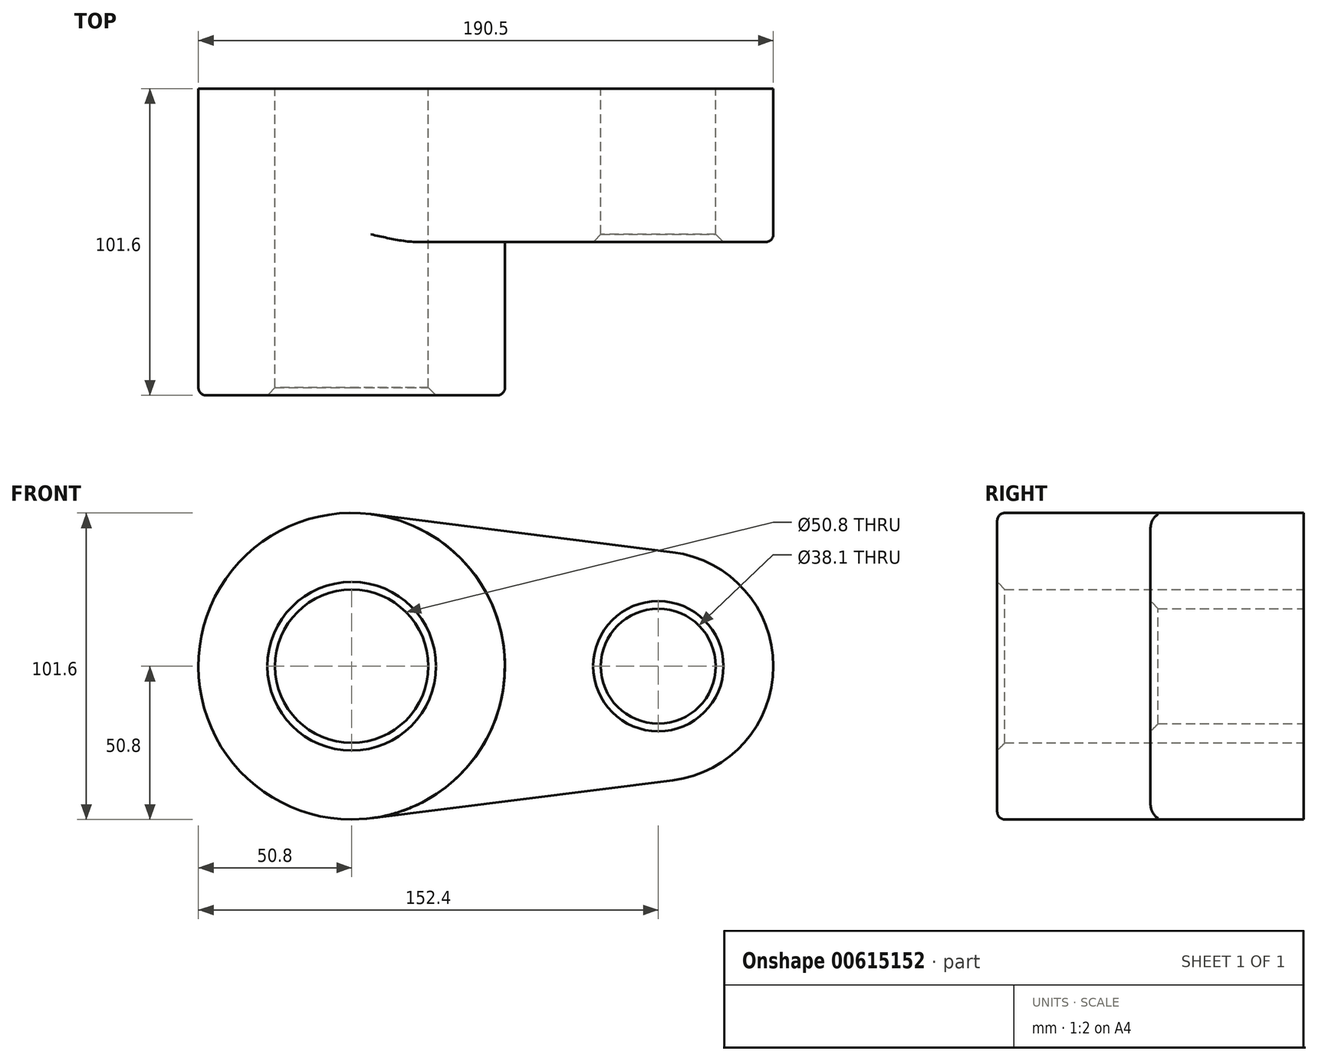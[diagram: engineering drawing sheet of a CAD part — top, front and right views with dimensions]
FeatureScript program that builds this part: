
annotation { "Feature Type Name" : "Feature", "Feature Type Description" : "" }
export const myFeature = defineFeature(function(context is Context, id is Id, definition is map)
    precondition{}
    {
        {
            var Q0;
            Q0=qCreatedBy(makeId("Front.planeOp"),FACE);
            var sketch = newSketch(context, id + "F0", { "sketchPlane" : qUnion([Q0])});
            skCircle(sketch, "E0", {"center": v(0, 0) * mm, "radius": 50.8 * mm});
            skCircle(sketch, "E1", {"center": v(101.6, 0) * mm, "radius": 38.1 * mm});
            skLineSegment(sketch, "E2", {"start": v(6.35, 50.4) * mm, "end": v(106.36, 37.8) * mm});
            skLineSegment(sketch, "E3", {"start": v(6.35, -50.4) * mm, "end": v(106.36, -37.8) * mm});
            skCircle(sketch, "E4", {"center": v(0, 0) * mm, "radius": 25.4 * mm});
            skCircle(sketch, "E5", {"center": v(101.6, 0) * mm, "radius": 19.05 * mm});
            skSolve(sketch);
        }
        {
            var Q0;
            Q0 = qSketchRegion(id + "F0", true);
            extrude(context, id + "F1", {"entities" : qUnion([Q0]), "depth" : 50.8 * mm, "offsetDistance" : 25.4 * mm});
        }
        {
            var Q0;
            Q0=makeQuery(id+"F0.imprint","IMPRINT",FACE,{"disambiguationData":[TD([[makeQuery(id+"F0.imprint","IMPRINT",EDGE,{"derivedFrom":sQuery(id+"F0.wireOp",EDGE,"E4")}),-1.0]])]});
            extrude(context, id + "F2", {"entities" : qUnion([Q0]), "operationType" : NewBodyOperationType.ADD, "depth" : 101.6 * mm, "offsetDistance" : 25.4 * mm});
        }
        {
            var Q0;
            Q0=makeQuery(id+"F1.opExtrude","CAP_EDGE",EDGE,{"disambiguationData":[OSD([sQuery(id+"F0.wireOp",EDGE,"E3")])],"isStart":false});
            var Q1;
            Q1=makeQuery(id+"F2.opExtrude","CAP_EDGE",EDGE,{"disambiguationData":[OSD([sQuery(id+"F0.wireOp",EDGE,"E0")])],"isStart":false});
            fillet(context, id + "F3", {"entities" : qUnion([Q0, Q1]), "tangentPropagation" : true, "radius" : 2.54 * mm, "defaultsChanged" : false, "vertexSettings" : [], "allowEdgeOverflow" : false});
        }
        {
            var Q0;
            Q0=makeQuery(id+"F2.opExtrude","CAP_EDGE",EDGE,{"disambiguationData":[OSD([sQuery(id+"F0.wireOp",EDGE,"E4")])],"isStart":false});
            var Q1;
            Q1=makeQuery(id+"F1.opExtrude","CAP_EDGE",EDGE,{"disambiguationData":[OSD([sQuery(id+"F0.wireOp",EDGE,"E5")])],"isStart":false});
            chamfer(context, id + "F4", {"entities" : qUnion([Q0, Q1]), "width" : 2.54 * mm, "tangentPropagation" : true});
        }
    });
